# Revit family: Sink-Main Bowl-Clark Cellini Undermount1
name_source: partatom
category: Plumbing Fixtures
revit_build: Autodesk Revit Architecture 2012 (Build: 20110916_2132(x64)
units: mm (PartAtom-declared; Revit-internal decimal feet)

## types (1)
- Cellini
    Assembly Code = D2010410
    CW Connection = No
    Cost = 0 $
    Default Elevation = 0 mm  [stored 0 ft]
    Depth_ANZRS = 175 mm  [stored 0.574147 ft]
    Description = Cellino Main Bowl Undermount
    HW Connection = No
    Keynote = SK
    Length_ANZRS = 428 mm  [stored 1.4042 ft]
    Manufacturer = Clark
    Material_ANZRS = Metal-Stainless-Caroma
    Model = ERBU
    Type Comments = Includes timber board, SS draining basket and basket wastes, Bowl Volume 20L, Carton size 530 x 520 x 190, Carton weight 3kg, Match with Dorf Neo Mixer range
    URL = http://www.clark.com.au
    Vent Connection = No
    WFU = 2
    Waste Connection = Yes
    Waste Radius = 25 mm  [stored 0.082021 ft]
    Width_ANZRS = 428 mm  [stored 1.4042 ft]

note: [stored X ft] marks values corroborated as IEEE doubles in the binary element streams (Revit-internal decimal feet)

## geometry (parser evidence)
native form markers: Blend x6, Sweep x2
no freeform markers — native parametric forms only
